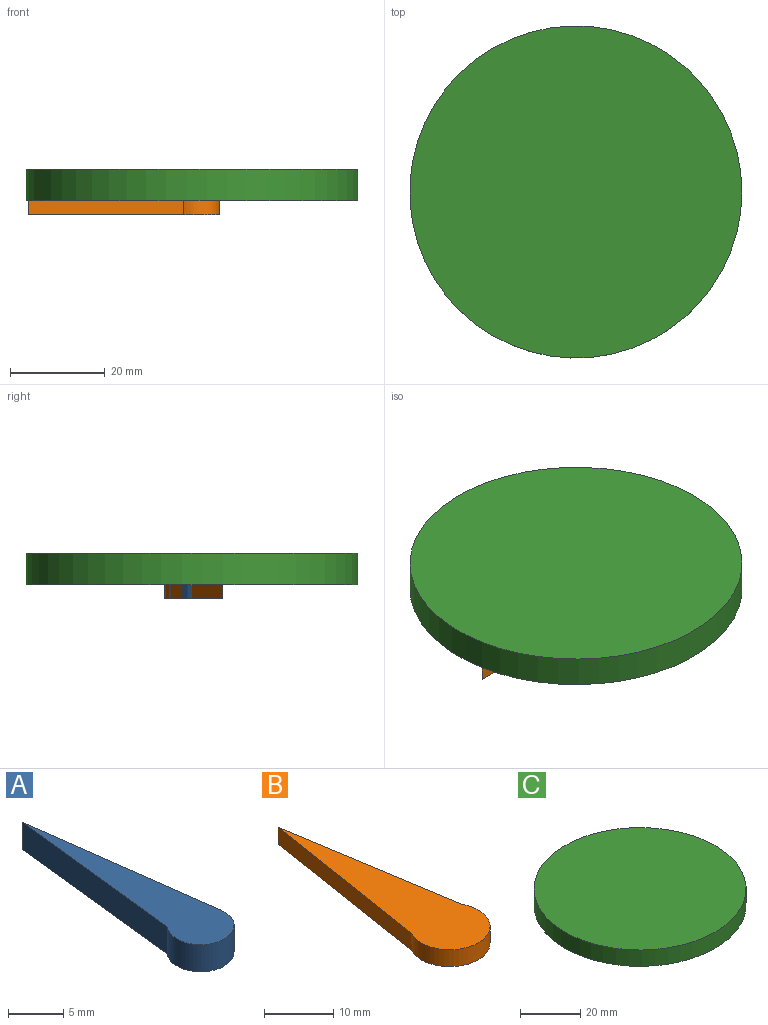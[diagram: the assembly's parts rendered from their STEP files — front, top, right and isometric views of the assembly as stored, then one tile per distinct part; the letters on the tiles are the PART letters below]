
ASSEMBLY  parts=3 mates=2
PART A: 5 faces, bbox 6x25.9x3 mm
  f0: cylinder r=3.02mm len=6.04mm, axis (0,0,-1), area 37.2mm2, adj f1,f2,f3,f4
  f1: plane 22.06x3mm, normal (0.99,0.13,0), area 66.7mm2, adj f0,f2,f3,f4
  f2: plane 20.9x3mm, normal (-0.99,0.11,0), area 63.1mm2, adj f0,f1,f3,f4
  f3: plane 25.86x6.04mm, normal (0,0,1), area 78.5mm2, adj f0,f1,f2
  f4: plane 25.86x6.04mm, normal (0,0,-1), area 78.5mm2, adj f0,f1,f2
PART B: 5 faces, bbox 11.7x41x3 mm
  f0: cylinder r=5.83mm len=11.67mm, axis (0,0,-1), area 72mm2, adj f1,f2,f3,f4
  f1: plane 32.36x5.14mm, normal (0.99,0.16,0), area 98.3mm2, adj f0,f2,f3,f4
  f2: plane 32.43x5.17mm, normal (-0.99,0.16,0), area 98.5mm2, adj f0,f1,f3,f4
  f3: plane 40.96x11.67mm, normal (0,0,1), area 251mm2, adj f0,f1,f2
  f4: plane 40.96x11.67mm, normal (0,0,-1), area 251mm2, adj f0,f1,f2
PART C: 3 faces, bbox 70.3x70.3x6.6 mm
  f0: cylinder r=35.13mm len=70.25mm, axis (0,0,-1), area 1457.6mm2, adj f1,f2
  f1: plane 70.25x70.25mm, normal (0,0,1), area 3876.5mm2, adj f0
  f2: plane 70.25x70.25mm, normal (0,0,-1), area 3876.5mm2, adj f0
PLACE A rot(axis=(0,0,1),87.6deg) t=(-14.49,-12.77,-14.41)mm
PLACE B rot(axis=(0,0,1),100.7deg) t=(-14.49,-12.77,-21.02)mm
PLACE C t=(-14.49,-12.77,-11.41)mm fixed
MATE revolute A.f0 <-> C.f0  axis (0,0,1) through (-14.49,-12.77,-11.41)mm
MATE revolute C.f0 <-> B.f0  axis (0,0,-1) through (-14.49,-12.77,-11.41)mm
